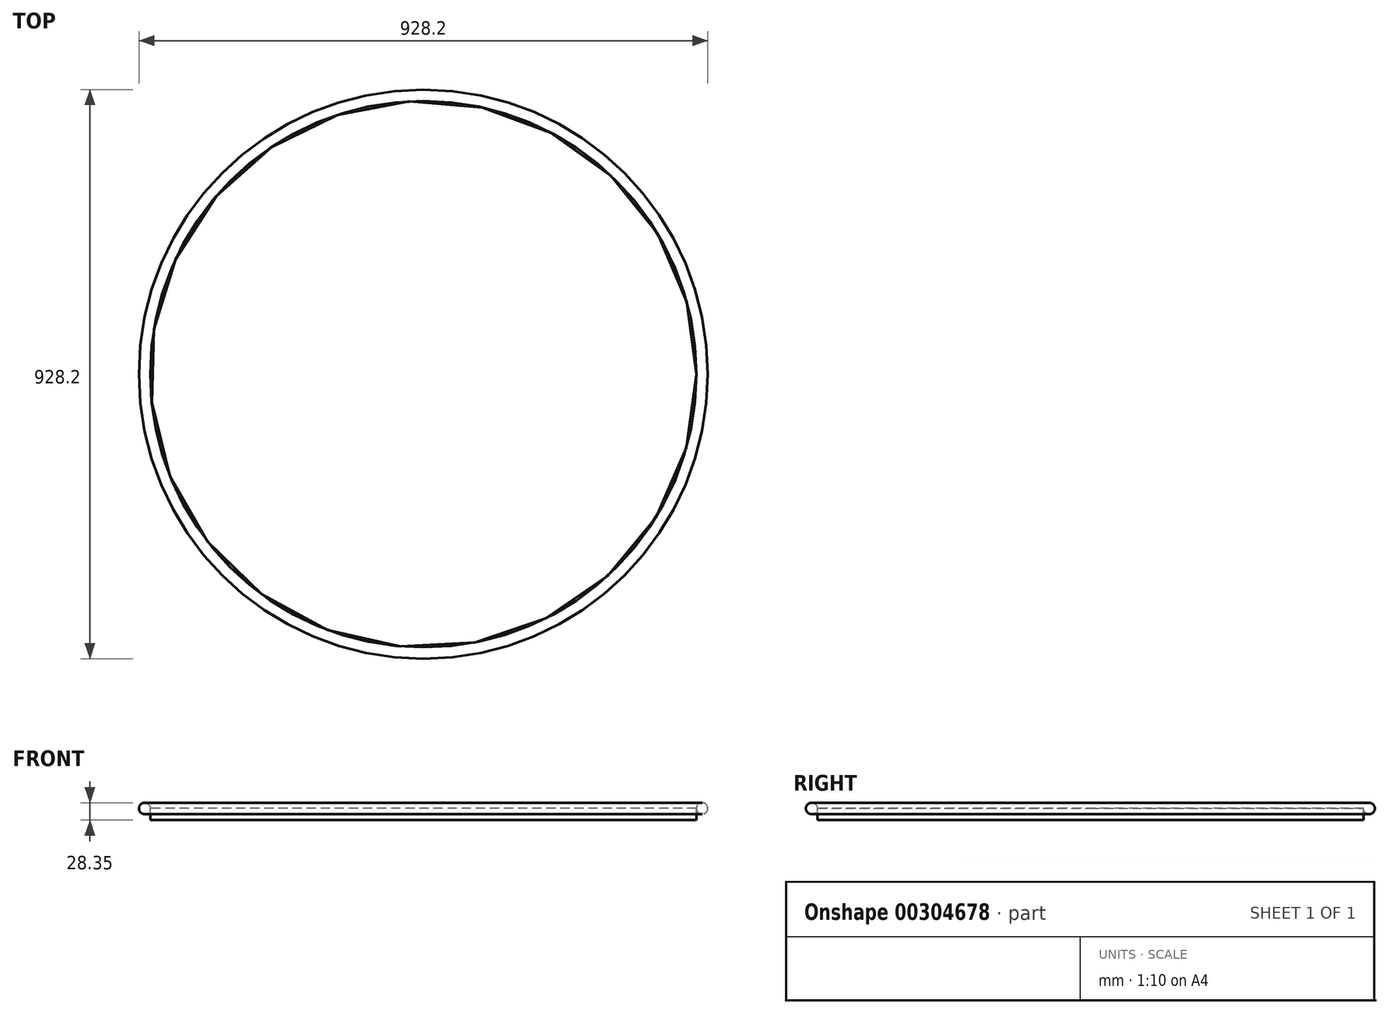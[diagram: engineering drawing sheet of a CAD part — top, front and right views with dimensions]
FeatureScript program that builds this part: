
annotation { "Feature Type Name" : "Feature", "Feature Type Description" : "" }
export const myFeature = defineFeature(function(context is Context, id is Id, definition is map)
    precondition{}
    {
        {
            var Q0;
            Q0=qCreatedBy(makeId("Top.planeOp"),FACE);
            var sketch = newSketch(context, id + "F0", { "sketchPlane" : qUnion([Q0])});
            skCircle(sketch, "E0", {"center": v(0, 0) * mm, "radius": 445.5 * mm});
            skSolve(sketch);
        }
        {
            var Q0;
            Q0=makeQuery(id+"F0.imprint","IMPRINT",FACE,{"disambiguationData":[TD([[makeQuery(id+"F0.imprint","IMPRINT",EDGE,{"derivedFrom":sQuery(id+"F0.wireOp",EDGE,"E0")}),1.0]])]});
            var sketch = newSketch(context, id + "F1", { "sketchPlane" : qUnion([Q0])});
            skCircle(sketch, "E1.0", {"center": v(0, 0) * mm, "radius": 464.1 * mm});
            skSolve(sketch);
        }
        {
            var Q0;
            Q0=makeQuery(id+"F1.imprint","IMPRINT",FACE,{"disambiguationData":[TD([[makeQuery(id+"F1.imprint","IMPRINT",EDGE,{"derivedFrom":makeQuery(id+"F0.imprint","IMPRINT",EDGE,{"derivedFrom":sQuery(id+"F0.wireOp",EDGE,"E0")})}),1.0]])]});
            var sketch = newSketch(context, id + "F2", { "sketchPlane" : qUnion([Q0])});
            skCircle(sketch, "E2.0", {"center": v(0, 0) * mm, "radius": 514.9 * mm});
            skSolve(sketch);
        }
        {
            var Q0;
            Q0=makeQuery(id+"F1.imprint","IMPRINT",FACE,{"disambiguationData":[TD([[makeQuery(id+"F1.imprint","IMPRINT",EDGE,{"derivedFrom":makeQuery(id+"F0.imprint","IMPRINT",EDGE,{"derivedFrom":sQuery(id+"F0.wireOp",EDGE,"E0")})}),1.0]])]});
            extrude(context, id + "F3", {"entities" : qUnion([Q0]), "oppositeDirection" : true, "depth" : 19.05 * mm});
        }
        {
            var Q0;
            Q0=qCreatedBy(makeId("Front.planeOp"),FACE);
            var sketch = newSketch(context, id + "F4", { "sketchPlane" : qUnion([Q0])});
            skLineSegment(sketch, "E3", {"start": v(0, 0) * mm, "end": v(0, 222.26) * mm, "construction": true});
            skLineSegment(sketch, "E4.0.0", {"start": v(-445.5, 0) * mm, "end": v(445.5, 0) * mm, "construction": true});
            skLineSegment(sketch, "E5", {"start": v(-445.5, 0) * mm, "end": v(-464.1, 0) * mm, "construction": true});
            skCircle(sketch, "E6", {"center": v(-454.8, 0) * mm, "radius": 9.3 * mm});
            skLineSegment(sketch, "E7", {"start": v(464.1, 0) * mm, "end": v(445.5, 0) * mm, "construction": true});
            skSolve(sketch);
        }
        {
            var Q0;
            Q0=makeQuery(id+"F4.imprint","IMPRINT",FACE,{"disambiguationData":[TD([[makeQuery(id+"F4.imprint","IMPRINT",EDGE,{"derivedFrom":sQuery(id+"F4.wireOp",EDGE,"E6")}),1.0]])]});
            var Q1;
            Q1=sQuery(id+"F4.wireOp",EDGE,"E3");
            revolve(context, id + "F5", {"entities" : qUnion([Q0]), "axis" : qUnion([Q1]), "revolveType" : RevolveType.FULL, "oppositeDirection" : true});
        }
    });
